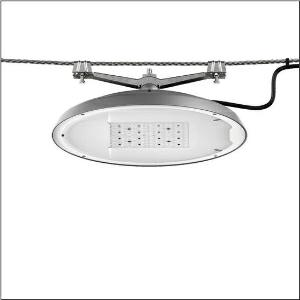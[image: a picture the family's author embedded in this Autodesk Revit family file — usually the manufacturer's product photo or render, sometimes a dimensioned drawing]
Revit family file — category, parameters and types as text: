
# Revit family: dl_r__50_iq_mini___st0_8s_5xa248v31f08me_3f47
name_source: partatom
category: Lighting Fixtures
units: mm (PartAtom-declared; Revit-internal decimal feet)

## family parameters
Cut with Voids When Loaded = No
Host = Face
Light Source = No
Part Type = Normal
Room Calculation Point = No
Round Connector Dimension = Use Diameter
Shared = No

## types (1)
- --- (1 x LED, 15660 lm, 107.8 W, 3000K)
    Apparent Load = 108 VA
    CIE Flux Codes = 38 75 97 100 100
    Color Rendering = 70
    Color Temperature = 3000K
    Default Elevation = 1800 mm
    Description = DL® 50 iQ mini, catenary luminaire, primary light control with lens, of PMMA, primary optical cover: cover, of toughened safety glass, transparent, light distribution: ST0.8s, light emission: direct distribution, primary light characteristic: symmetric, installation type: suspended mounting, LED, High Power LED, rated luminous flux: 15.660lm, luminous efficacy: 145lm/W, light colour: 730, colour temperature: 3000K, control: optimised constant luminous flux control (CLO 2.0), Desk-Remote (wireless, voltage-free reading and setting of iQ features in the workshop via application-optimized NFC function/RFID function), Light-Fading, Smart-Wire, Night-Set, Lumen-Switch, Temp-Guard, Auto-Match, Street-Remote, mains connection: 230..240V, AC, 50/60Hz, start of lifetime: 108W, end of service life: 118W, reduction: 47W, luminaire housing, of diecast aluminium, powder-coated, Siteco® metallic grey (DB 702S), diameter: 500mm, height: 115mm, protection rating (complete): IP66, insulation class (complete): insulation class II (safety insulation), certification: CE, ENEC, VDE, impact resistance: IK08, permissible operating ambient temperature for outdoor applications: -25..+40°C, standard-compliant lighting for roads and squares, packaging unit: 1 piece

Light Distribution: ST0.8s
    Height = 124 mm  [stored 0.406824 ft]
    Lamp = 1 x LED
    Lamp Light Flux = 15660 lm
    Lamp Power = 107.8 W
    Lamp count = 1
    Length = 500 mm
    Luminous efficacy = 145 lm/W
    Manufacturer = Siteco
    ModVariant = No
    Model = 5XA248V31F08ME
    Number of Poles = 1
    OnlyDefault = Yes
    Power Factor = 1
    Product Name = DL® 50 iQ mini | ST0.8s
    Product group = catenary luminaire
    ProductGroupID = 6300
    Protection Class = Protection class II
    Protection Degree = IP 66
    RLX_Detail_Level = 1
    RLX_Emergency_Light_Flux = 0 lm
    RLX_Emergency_Type = 0
    RLX_Emergency_Type_DB = No
    RlxData = <blob elided: 126841 chars, md5=2095511c>
    Socket = socket
    Standby Power = 0 W
    System Light Flux = 15660 lm
    System Power = 108 W
    Type Comments = factory setting: luminous flux: 100 % | dim-lin: 254 | 565 mA
    Type Image = l_1251783.jpg
    URL = http://relux.com
    VarID = @adj_072307
    Voltage = 0 V
    Weight = 0.00 kg
    Width = 0 mm  [stored 0 ft]

note: [stored X ft] marks values corroborated as IEEE doubles in the binary element streams (Revit-internal decimal feet)

## geometry (parser evidence)
native form markers: Blend x4, Sweep x15
no freeform markers — native parametric forms only
